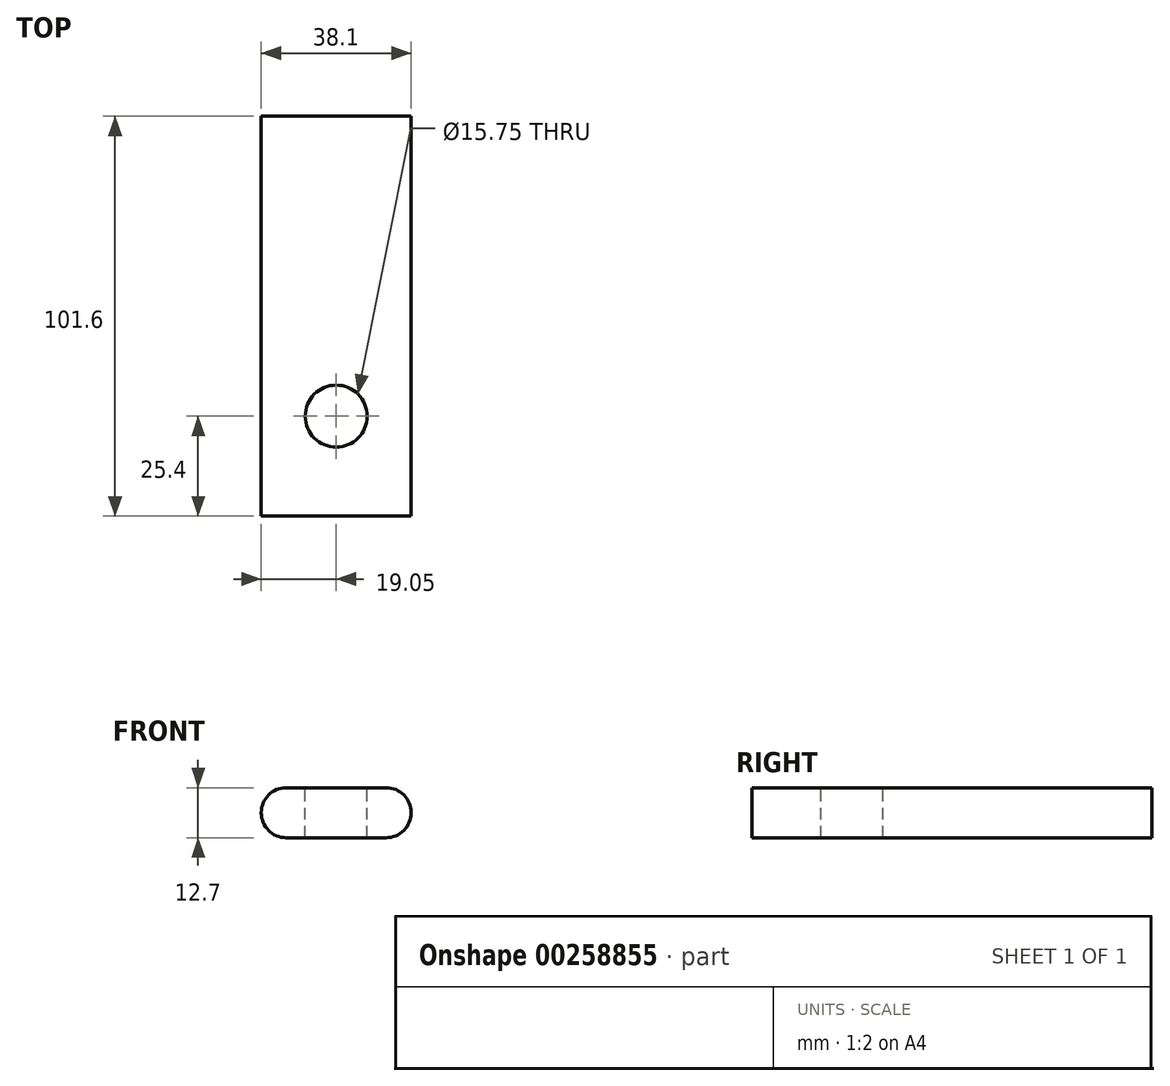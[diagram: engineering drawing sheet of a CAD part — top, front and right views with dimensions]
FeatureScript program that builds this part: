
annotation { "Feature Type Name" : "Feature", "Feature Type Description" : "" }
export const myFeature = defineFeature(function(context is Context, id is Id, definition is map)
    precondition{}
    {
        {
            var Q0;
            Q0=qCreatedBy(makeId("Front.planeOp"),FACE);
            var sketch = newSketch(context, id + "F0", { "sketchPlane" : qUnion([Q0])});
            skLineSegment(sketch, "E0.bottom", {"start": v(19.05, 6.35) * mm, "end": v(-19.05, 6.35) * mm});
            skLineSegment(sketch, "E0.top", {"start": v(19.05, -6.35) * mm, "end": v(-19.05, -6.35) * mm});
            skLineSegment(sketch, "E0.left", {"start": v(19.05, 6.35) * mm, "end": v(19.05, -6.35) * mm});
            skLineSegment(sketch, "E0.right", {"start": v(-19.05, 6.35) * mm, "end": v(-19.05, -6.35) * mm});
            skPoint(sketch, "E0.middle", {"position": v(0, 0) * mm});
            skSolve(sketch);
        }
        {
            var Q0;
            Q0 = qSketchRegion(id + "F0", true);
            extrude(context, id + "F1", {"entities" : qUnion([Q0]), "endBound" : BoundingType.SYMMETRIC, "depth" : 101.6 * mm});
        }
        {
            var Q0;
            Q0=makeQuery(id+"F1.opExtrude","SWEPT_EDGE",EDGE,{"disambiguationData":[OSD([sQuery(id+"F0.wireOp",EDGE,"E0.bottom"),sQuery(id+"F0.wireOp",EDGE,"E0.right")])]});
            var Q1;
            Q1=makeQuery(id+"F1.opExtrude","SWEPT_EDGE",EDGE,{"disambiguationData":[OSD([sQuery(id+"F0.wireOp",EDGE,"E0.bottom"),sQuery(id+"F0.wireOp",EDGE,"E0.left")])]});
            var Q2;
            Q2=makeQuery(id+"F1.opExtrude","SWEPT_EDGE",EDGE,{"disambiguationData":[OSD([sQuery(id+"F0.wireOp",EDGE,"E0.top"),sQuery(id+"F0.wireOp",EDGE,"E0.left")])]});
            var Q3;
            Q3=makeQuery(id+"F1.opExtrude","SWEPT_EDGE",EDGE,{"disambiguationData":[OSD([sQuery(id+"F0.wireOp",EDGE,"E0.top"),sQuery(id+"F0.wireOp",EDGE,"E0.right")])]});
            fillet(context, id + "F2", {"entities" : qUnion([Q0, Q1, Q2, Q3]), "radius" : 6.35 * mm, "tangentPropagation" : true, "allowEdgeOverflow" : false});
        }
        {
            var Q0;
            Q0=makeQuery(id+"F1.opExtrude","SWEPT_FACE",FACE,{"disambiguationData":[OSD([sQuery(id+"F0.wireOp",EDGE,"E0.bottom")])]});
            var sketch = newSketch(context, id + "F3", { "sketchPlane" : qUnion([Q0])});
            skCircle(sketch, "E1", {"center": v(0, -25.4) * mm, "radius": 7.87 * mm});
            skSolve(sketch);
        }
        {
            var Q0;
            Q0=makeQuery(id+"F3.imprint","IMPRINT",FACE,{"disambiguationData":[TD([[makeQuery(id+"F3.imprint","IMPRINT",EDGE,{"derivedFrom":sQuery(id+"F3.wireOp",EDGE,"E1")}),1.0]])]});
            extrude(context, id + "F4", {"entities" : qUnion([Q0]), "operationType" : NewBodyOperationType.REMOVE, "endBound" : BoundingType.THROUGH_ALL, "oppositeDirection" : true, "depth" : 25.4 * mm});
        }
    });
